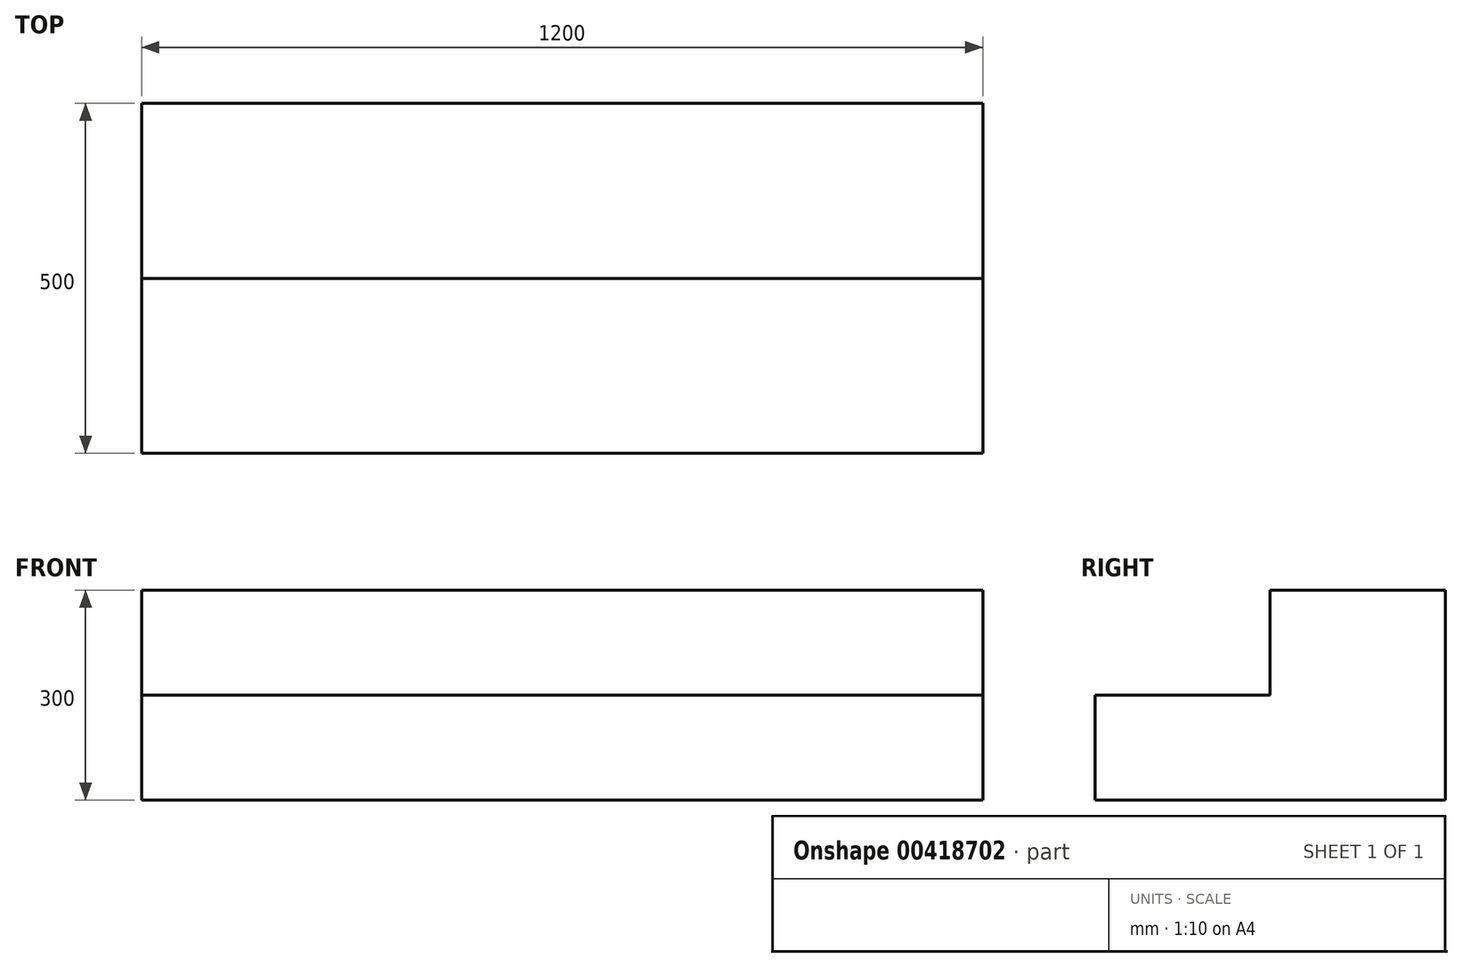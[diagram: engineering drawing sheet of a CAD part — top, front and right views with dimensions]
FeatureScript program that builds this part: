
annotation { "Feature Type Name" : "Feature", "Feature Type Description" : "" }
export const myFeature = defineFeature(function(context is Context, id is Id, definition is map)
    precondition{}
    {
        {
            var Q0;
            Q0=qCreatedBy(makeId("Right.planeOp"),FACE);
            var sketch = newSketch(context, id + "F0", { "sketchPlane" : qUnion([Q0])});
            skLineSegment(sketch, "E0", {"start": v(0, 0) * mm, "end": v(0, 300) * mm});
            skLineSegment(sketch, "E1", {"start": v(0, 300) * mm, "end": v(-250, 300) * mm});
            skLineSegment(sketch, "E2", {"start": v(-250, 300) * mm, "end": v(-250, 150) * mm});
            skLineSegment(sketch, "E3", {"start": v(-250, 150) * mm, "end": v(-500, 150) * mm});
            skLineSegment(sketch, "E4", {"start": v(-500, 150) * mm, "end": v(-500, 0) * mm});
            skLineSegment(sketch, "E5", {"start": v(-500, 0) * mm, "end": v(0, 0) * mm});
            skSolve(sketch);
        }
        {
            var Q0;
            Q0 = qSketchRegion(id + "F0", true);
            extrude(context, id + "F1", {"entities" : qUnion([Q0]), "endBound" : BoundingType.SYMMETRIC, "depth" : 1200 * mm, "offsetDistance" : 25 * mm});
        }
    });
